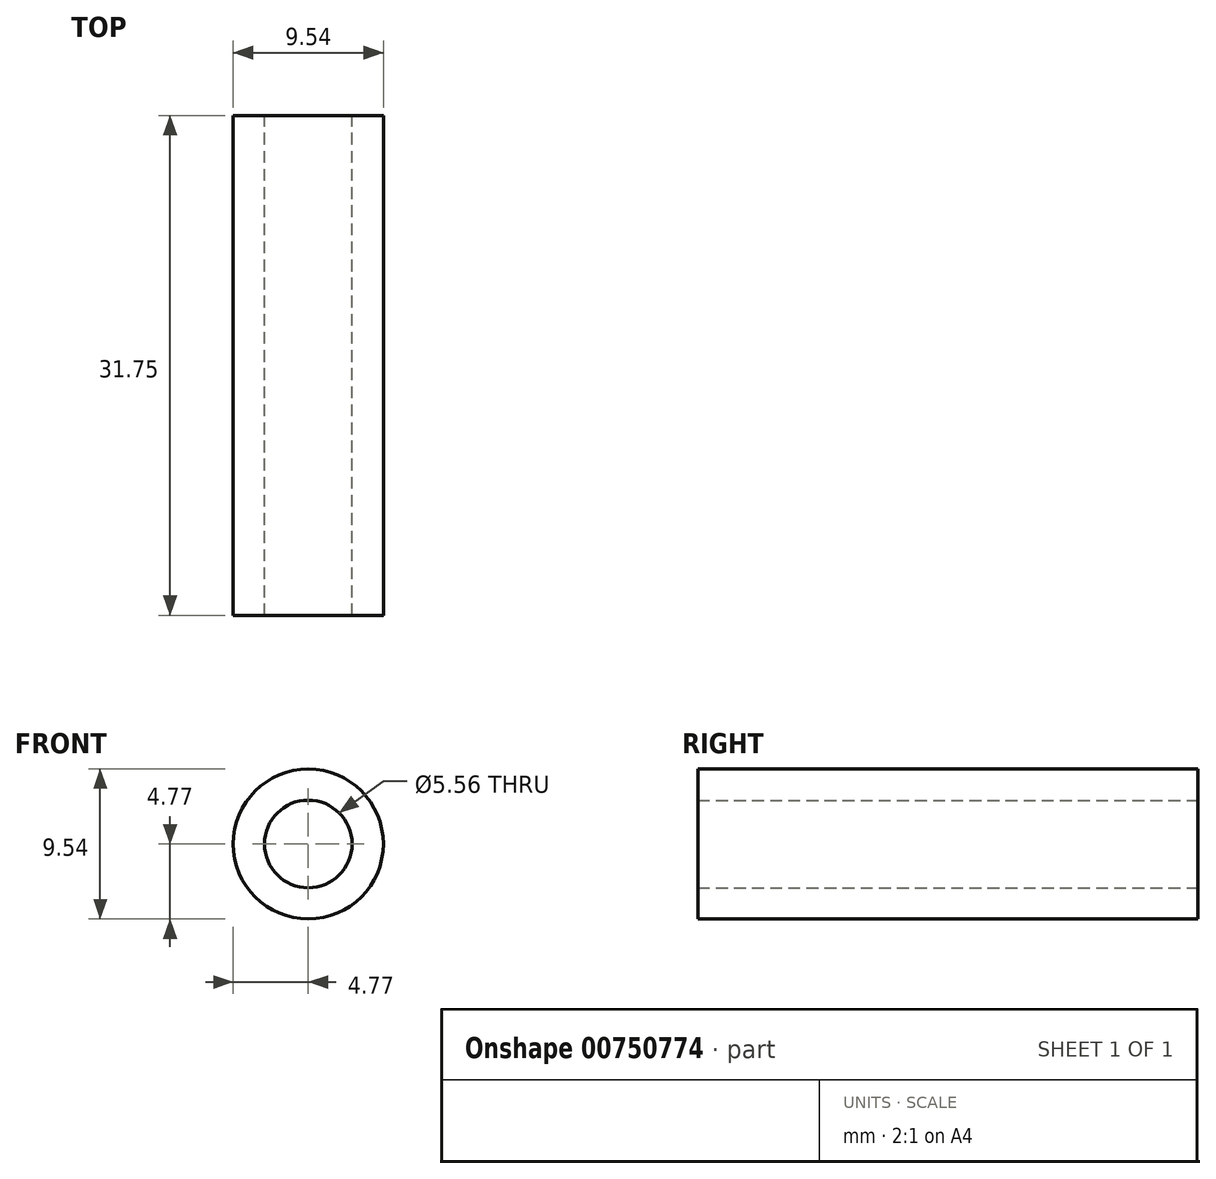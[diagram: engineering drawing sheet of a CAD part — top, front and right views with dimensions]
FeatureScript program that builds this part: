
annotation { "Feature Type Name" : "Feature", "Feature Type Description" : "" }
export const myFeature = defineFeature(function(context is Context, id is Id, definition is map)
    precondition{}
    {
        {
            var Q0;
            Q0=qCreatedBy(makeId("Front.planeOp"),FACE);
            var sketch = newSketch(context, id + "F0", { "sketchPlane" : qUnion([Q0])});
            skCircle(sketch, "E0", {"center": v(0, 0) * mm, "radius": 2.78 * mm});
            skCircle(sketch, "E1", {"center": v(0, 0) * mm, "radius": 4.77 * mm});
            skSolve(sketch);
        }
        {
            var Q0;
            Q0=qSketchRegion(id+"F0",true);
            extrude(context, id + "F1", {"entities" : qUnion([Q0]), "depth" : 31.75 * mm, "offsetDistance" : 25 * mm});
        }
    });
